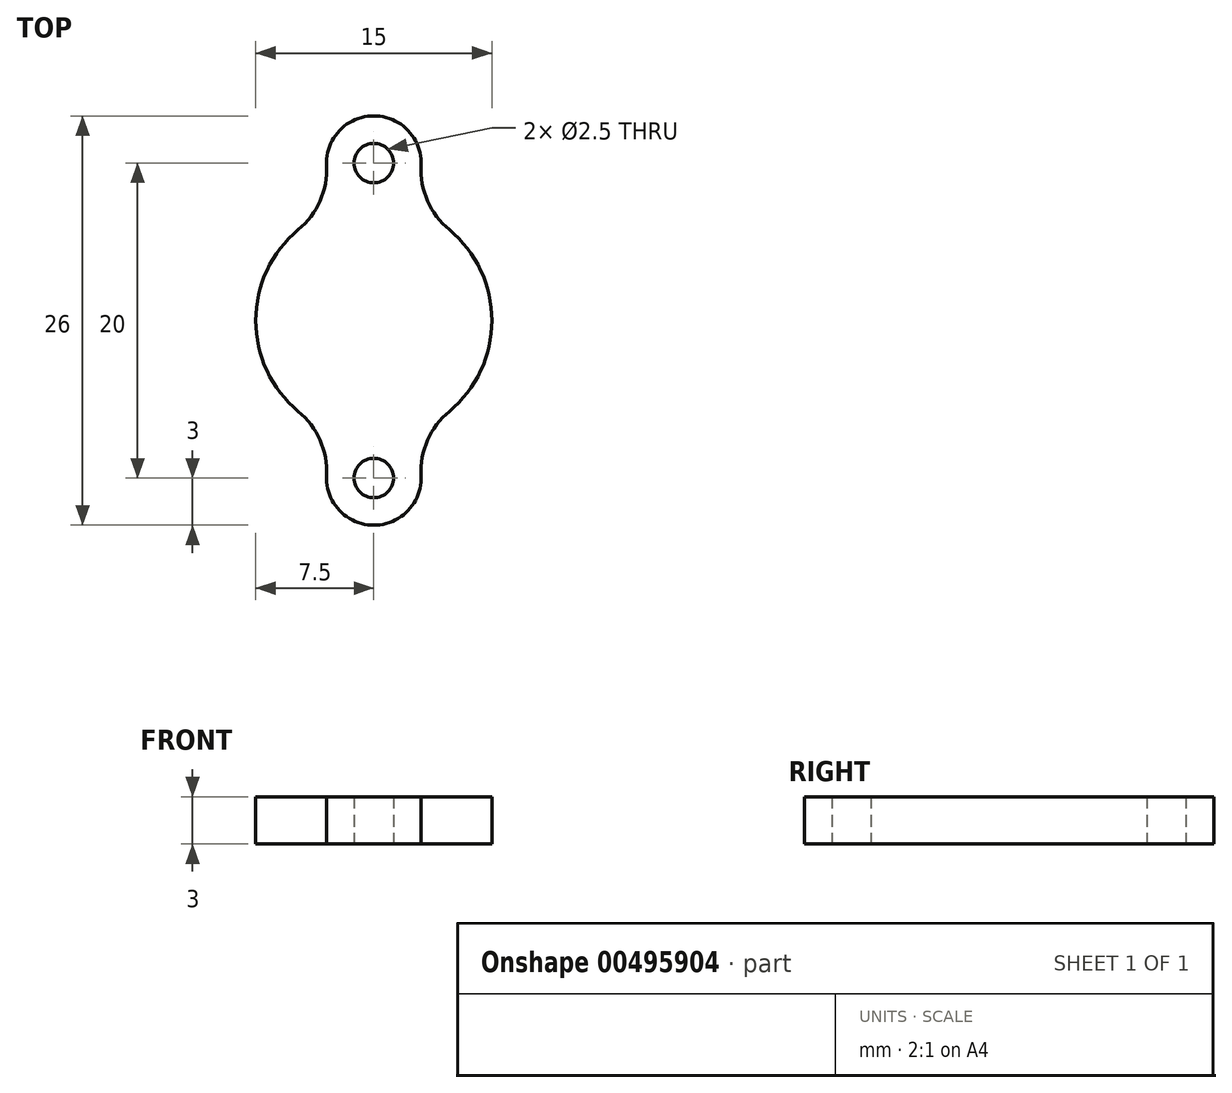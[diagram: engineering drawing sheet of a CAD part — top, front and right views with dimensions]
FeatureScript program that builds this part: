
annotation { "Feature Type Name" : "Feature", "Feature Type Description" : "" }
export const myFeature = defineFeature(function(context is Context, id is Id, definition is map)
    precondition{}
    {
        {
            var Q0;
            Q0=qCreatedBy(makeId("Top.planeOp"),FACE);
            var sketch = newSketch(context, id + "F0", { "sketchPlane" : qUnion([Q0])});
            skLineSegment(sketch, "E0", {"start": v(0, 10) * mm, "end": v(0, 0) * mm, "construction": true});
            skLineSegment(sketch, "E1", {"start": v(0, 0) * mm, "end": v(0, -10) * mm, "construction": true});
            skCircle(sketch, "E2", {"center": v(0, 10) * mm, "radius": 3 * mm});
            skCircle(sketch, "E3", {"center": v(0, -10) * mm, "radius": 3 * mm});
            skCircle(sketch, "E4", {"center": v(0, 0) * mm, "radius": 7.5 * mm});
            skSolve(sketch);
        }
        {
            var Q0;
            {var subQ0=sQuery(id+"F0.wireOp",EDGE,"E4");var subQ1=sQuery(id+"F0.wireOp",EDGE,"E2");var subQ2=makeQuery(id+"F0.imprint","INTERSECT",VERTEX,{"disambiguationData":[OD(0.0)],"derivedFrom":[subQ1,subQ0]});Q0=makeQuery(id+"F0.imprint","IMPRINT",FACE,{"disambiguationData":[TD([[makeQuery(id+"F0.imprint","IMPRINT",EDGE,{"disambiguationData":[TD([[subQ2,1.0]])],"derivedFrom":subQ1}),1.0]])]});}
            var Q1;
            {var subQ0=sQuery(id+"F0.wireOp",EDGE,"E4");var subQ1=sQuery(id+"F0.wireOp",EDGE,"E3");var subQ2=makeQuery(id+"F0.imprint","INTERSECT",VERTEX,{"disambiguationData":[OD(0.0)],"derivedFrom":[subQ1,subQ0]});Q1=makeQuery(id+"F0.imprint","IMPRINT",FACE,{"disambiguationData":[TD([[makeQuery(id+"F0.imprint","IMPRINT",EDGE,{"disambiguationData":[TD([[subQ2,-1.0]])],"derivedFrom":subQ1}),1.0]])]});}
            var Q2;
            {var subQ0=sQuery(id+"F0.wireOp",EDGE,"E4");var subQ1=sQuery(id+"F0.wireOp",EDGE,"E2");var subQ2=makeQuery(id+"F0.imprint","INTERSECT",VERTEX,{"disambiguationData":[OD(0.0)],"derivedFrom":[subQ1,subQ0]});Q2=makeQuery(id+"F0.imprint","IMPRINT",FACE,{"disambiguationData":[TD([[makeQuery(id+"F0.imprint","IMPRINT",EDGE,{"disambiguationData":[TD([[subQ2,-1.0]])],"derivedFrom":subQ1}),-1.0]])]});}
            var Q3;
            {var subQ0=sQuery(id+"F0.wireOp",EDGE,"E4");var subQ1=sQuery(id+"F0.wireOp",EDGE,"E2");var subQ2=makeQuery(id+"F0.imprint","INTERSECT",VERTEX,{"disambiguationData":[OD(0.0)],"derivedFrom":[subQ1,subQ0]});Q3=makeQuery(id+"F0.imprint","IMPRINT",FACE,{"disambiguationData":[TD([[makeQuery(id+"F0.imprint","IMPRINT",EDGE,{"disambiguationData":[TD([[subQ2,-1.0]])],"derivedFrom":subQ1}),1.0]])]});}
            var Q4;
            {var subQ0=sQuery(id+"F0.wireOp",EDGE,"E4");var subQ1=sQuery(id+"F0.wireOp",EDGE,"E3");var subQ2=makeQuery(id+"F0.imprint","INTERSECT",VERTEX,{"disambiguationData":[OD(0.0)],"derivedFrom":[subQ1,subQ0]});Q4=makeQuery(id+"F0.imprint","IMPRINT",FACE,{"disambiguationData":[TD([[makeQuery(id+"F0.imprint","IMPRINT",EDGE,{"disambiguationData":[TD([[subQ2,1.0]])],"derivedFrom":subQ1}),1.0]])]});}
            extrude(context, id + "F1", {"entities" : qUnion([Q0, Q1, Q2, Q3, Q4]), "depth" : 3 * mm});
        }
        {
            var Q0;
            {var subQ0=sQuery(id+"F0.wireOp",EDGE,"E4");var subQ1=sQuery(id+"F0.wireOp",EDGE,"E3");Q0=makeQuery(id+"F1.opExtrude","SWEPT_EDGE",EDGE,{"disambiguationData":[OSD([subQ1,subQ0]),TDD([makeQuery(id+"F0.imprint","INTERSECT",VERTEX,{"disambiguationData":[OD(1.0)],"derivedFrom":[subQ1,subQ0]})])]});}
            var Q1;
            {var subQ0=sQuery(id+"F0.wireOp",EDGE,"E4");var subQ1=sQuery(id+"F0.wireOp",EDGE,"E3");Q1=makeQuery(id+"F1.opExtrude","SWEPT_EDGE",EDGE,{"disambiguationData":[OSD([subQ1,subQ0]),TDD([makeQuery(id+"F0.imprint","INTERSECT",VERTEX,{"disambiguationData":[OD(0.0)],"derivedFrom":[subQ1,subQ0]})])]});}
            var Q2;
            {var subQ0=sQuery(id+"F0.wireOp",EDGE,"E4");var subQ1=sQuery(id+"F0.wireOp",EDGE,"E2");Q2=makeQuery(id+"F1.opExtrude","SWEPT_EDGE",EDGE,{"disambiguationData":[OSD([subQ1,subQ0]),TDD([makeQuery(id+"F0.imprint","INTERSECT",VERTEX,{"disambiguationData":[OD(0.0)],"derivedFrom":[subQ1,subQ0]})])]});}
            var Q3;
            {var subQ0=sQuery(id+"F0.wireOp",EDGE,"E4");var subQ1=sQuery(id+"F0.wireOp",EDGE,"E2");Q3=makeQuery(id+"F1.opExtrude","SWEPT_EDGE",EDGE,{"disambiguationData":[OSD([subQ1,subQ0]),TDD([makeQuery(id+"F0.imprint","INTERSECT",VERTEX,{"disambiguationData":[OD(1.0)],"derivedFrom":[subQ1,subQ0]})])]});}
            fillet(context, id + "F2", {"entities" : qUnion([Q0, Q1, Q2, Q3]), "radius" : 5 * mm, "tangentPropagation" : true, "allowEdgeOverflow" : false});
        }
        {
            var Q0;
            Q0=sQuery(id+"F0.wireOp",VERTEX,"E1.end");
            var Q1;
            Q1=sQuery(id+"F0.wireOp",VERTEX,"E0.start");
            var Q2;
            Q2=makeQuery(id+"F1.opExtrude","SWEPT_BODY",BODY,{"disambiguationData":[OSD([sQuery(id+"F0.wireOp",EDGE,"E2"),sQuery(id+"F0.wireOp",EDGE,"E3"),sQuery(id+"F0.wireOp",EDGE,"E4")])]});
            hole(context, id + "F3", {"style" : HoleStyle.SIMPLE, "endStyle" : HoleEndStyle.THROUGH, "oppositeDirection" : true, "holeDiameter" : 2.5 * mm, "tappedDepth" : 12 * mm, "tapClearance" : 3, "locations" : qUnion([Q0, Q1]), "scope" : qUnion([Q2])});
        }
    });
